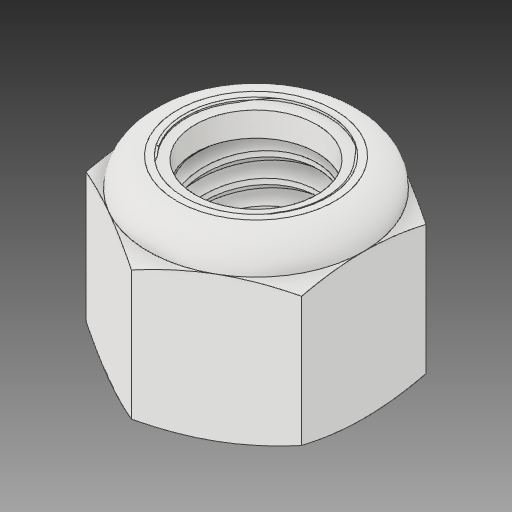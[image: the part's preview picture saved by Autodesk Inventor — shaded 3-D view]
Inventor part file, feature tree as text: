
AUTODESK INVENTOR PART (.ipt)
format: ipt  version: 2017.1 (Build 211199000, 199)  size: 375,296 bytes
history: native  units: in
note: dims shown in document units (in); Inventor stores cm internally (conversion verified against a paired STEP export)
features: other x1, revolve x1
ambient origin geometry x8: Origin, YZ Plane, XZ Plane, XY Plane, X Axis, Y Axis, Z Axis, Center Point
bodies: Solid1 (feature_tree), Solid2 (feature_tree)
feature tree (2):
  other  "Cut-Revolve4"
  revolve  "Revolve2"  [1 undecoded]
note: 1 required parameter value undecoded (feature->parameter linkage not recoverable at this tier; creation-order binding heuristic only, values carry confidence <= 0.55)
